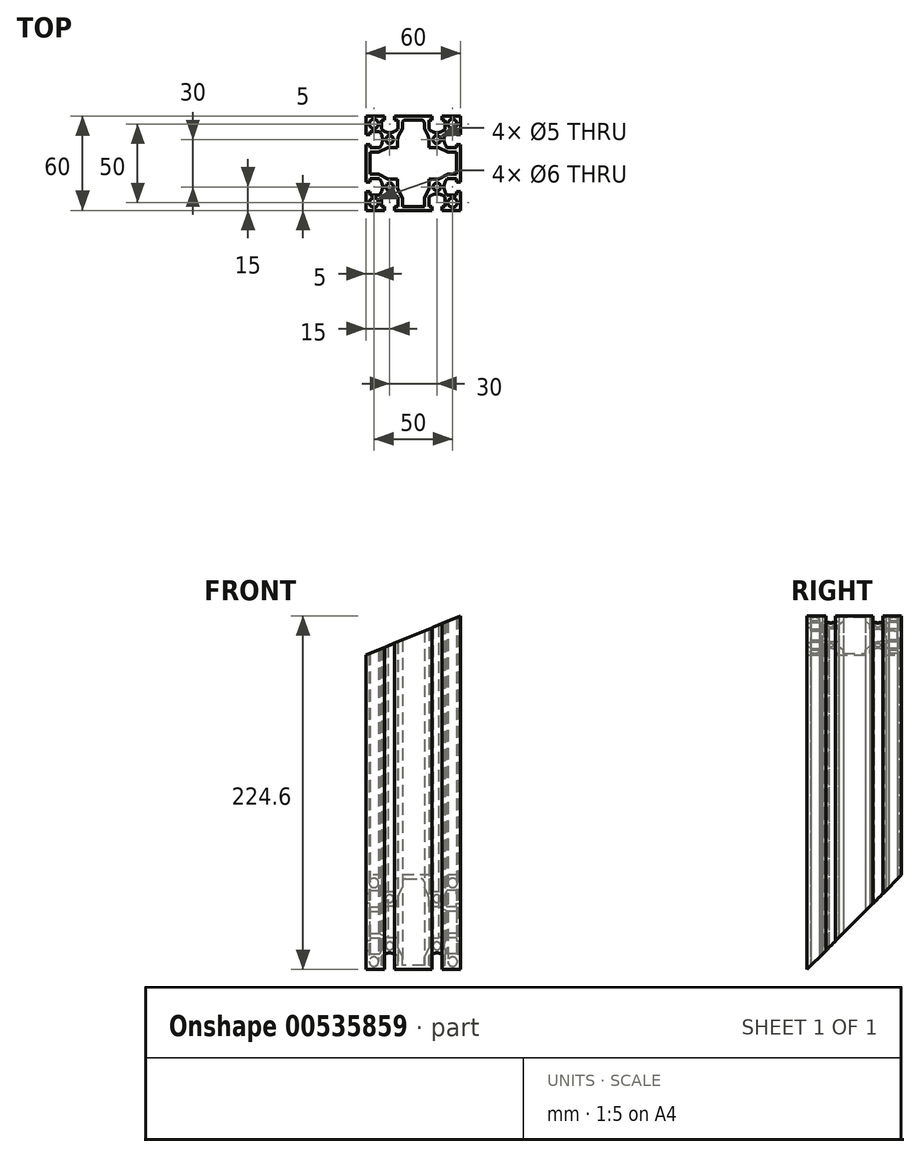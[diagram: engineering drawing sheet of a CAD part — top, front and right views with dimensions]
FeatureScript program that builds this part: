
annotation { "Feature Type Name" : "Feature", "Feature Type Description" : "" }
export const myFeature = defineFeature(function(context is Context, id is Id, definition is map)
    precondition{}
    {
        {
            var Q0;
            Q0=qCreatedBy(makeId("Top.planeOp"),FACE);
            var sketch = newSketch(context, id + "F0", { "sketchPlane" : qUnion([Q0])});
            skLineSegment(sketch, "E0.bottom", {"start": v(30, -30) * mm, "end": v(-30, -30) * mm});
            skLineSegment(sketch, "E0.top", {"start": v(30, 30) * mm, "end": v(-30, 30) * mm});
            skLineSegment(sketch, "E0.left", {"start": v(30, -30) * mm, "end": v(30, 30) * mm});
            skLineSegment(sketch, "E0.right", {"start": v(-30, -30) * mm, "end": v(-30, 30) * mm});
            skPoint(sketch, "E0.middle", {"position": v(0, 0) * mm});
            skLineSegment(sketch, "E1.top", {"start": v(-11.85, 30) * mm, "end": v(-18.15, 30) * mm});
            skLineSegment(sketch, "E1.left", {"start": v(-11.85, 27.5) * mm, "end": v(-11.85, 30) * mm});
            skLineSegment(sketch, "E1.right", {"start": v(-18.15, 27.5) * mm, "end": v(-18.15, 30) * mm});
            skPoint(sketch, "E1.middle", {"position": v(-15, 28.75) * mm});
            skLineSegment(sketch, "E2.bottom", {"start": v(-9.85, 27.5) * mm, "end": v(-11.85, 27.5) * mm});
            skLineSegment(sketch, "E2.left", {"start": v(-9.85, 27.5) * mm, "end": v(-9.85, 21.55) * mm});
            skLineSegment(sketch, "E2.right", {"start": v(-20.15, 27.5) * mm, "end": v(-20.15, 21.55) * mm});
            skPoint(sketch, "E2.middle", {"position": v(-15, 24.52) * mm});
            skArc(sketch, "E3", {"start": v(-20.15, 21.55) * mm, "mid": v(-15, 19.5) * mm, "end": v(-9.85, 21.55) * mm});
            skPoint(sketch, "E4.MirrorP", {"position": v(15, 24.52) * mm});
            skPoint(sketch, "E5.MirrorP", {"position": v(15, 28.75) * mm});
            skLineSegment(sketch, "E6.MirrorCS", {"start": v(11.85, 27.5) * mm, "end": v(11.85, 30) * mm});
            skLineSegment(sketch, "E7.MirrorCS", {"start": v(18.15, 27.5) * mm, "end": v(18.15, 30) * mm});
            skLineSegment(sketch, "E8.MirrorCS", {"start": v(9.85, 27.5) * mm, "end": v(11.85, 27.5) * mm});
            skLineSegment(sketch, "E9.MirrorCS", {"start": v(9.85, 27.5) * mm, "end": v(9.85, 21.55) * mm});
            skArc(sketch, "E10.MirrorCS", {"start": v(20.15, 21.55) * mm, "mid": v(15, 19.5) * mm, "end": v(9.85, 21.55) * mm});
            skLineSegment(sketch, "E11.MirrorCS", {"start": v(20.15, 27.5) * mm, "end": v(20.15, 21.55) * mm});
            skLineSegment(sketch, "E12.MirrorCS", {"start": v(11.85, 30) * mm, "end": v(18.15, 30) * mm});
            skLineSegment(sketch, "E13.1.0", {"start": v(27.5, 20.15) * mm, "end": v(21.55, 20.15) * mm});
            skLineSegment(sketch, "E13.1.1", {"start": v(27.5, 9.85) * mm, "end": v(21.55, 9.85) * mm});
            skArc(sketch, "E13.1.2", {"start": v(21.55, 20.15) * mm, "mid": v(19.5, 15) * mm, "end": v(21.55, 9.85) * mm});
            skLineSegment(sketch, "E13.1.3", {"start": v(27.5, -9.85) * mm, "end": v(21.55, -9.85) * mm});
            skLineSegment(sketch, "E13.1.4", {"start": v(27.5, -20.15) * mm, "end": v(21.55, -20.15) * mm});
            skPoint(sketch, "E13.1.5", {"position": v(28.75, 15) * mm});
            skPoint(sketch, "E13.1.6", {"position": v(28.75, -15) * mm});
            skArc(sketch, "E13.1.7", {"start": v(21.55, -20.15) * mm, "mid": v(19.5, -15) * mm, "end": v(21.55, -9.85) * mm});
            skPoint(sketch, "E13.1.8", {"position": v(24.52, -15) * mm});
            skPoint(sketch, "E13.1.9", {"position": v(24.52, 15) * mm});
            skLineSegment(sketch, "E13.1.10", {"start": v(27.5, 9.85) * mm, "end": v(27.5, 20.15) * mm});
            skLineSegment(sketch, "E13.1.11", {"start": v(27.5, -11.85) * mm, "end": v(27.5, -18.15) * mm});
            skLineSegment(sketch, "E13.1.12", {"start": v(30, 11.85) * mm, "end": v(30, 18.15) * mm});
            skLineSegment(sketch, "E13.1.13", {"start": v(30, -11.85) * mm, "end": v(30, -18.15) * mm});
            skLineSegment(sketch, "E13.1.14", {"start": v(27.5, 18.15) * mm, "end": v(30, 18.15) * mm});
            skLineSegment(sketch, "E13.1.15", {"start": v(27.5, 11.85) * mm, "end": v(30, 11.85) * mm});
            skLineSegment(sketch, "E13.1.16", {"start": v(27.5, 11.85) * mm, "end": v(27.5, 18.15) * mm});
            skLineSegment(sketch, "E13.1.17", {"start": v(27.5, -9.85) * mm, "end": v(27.5, -20.15) * mm});
            skLineSegment(sketch, "E13.1.18", {"start": v(27.5, -18.15) * mm, "end": v(30, -18.15) * mm});
            skLineSegment(sketch, "E13.1.19", {"start": v(27.5, -11.85) * mm, "end": v(30, -11.85) * mm});
            skLineSegment(sketch, "E13.2.0", {"start": v(20.15, -27.5) * mm, "end": v(20.15, -21.55) * mm});
            skLineSegment(sketch, "E13.2.1", {"start": v(9.85, -27.5) * mm, "end": v(9.85, -21.55) * mm});
            skArc(sketch, "E13.2.2", {"start": v(20.15, -21.55) * mm, "mid": v(15, -19.5) * mm, "end": v(9.85, -21.55) * mm});
            skLineSegment(sketch, "E13.2.3", {"start": v(-9.85, -27.5) * mm, "end": v(-9.85, -21.55) * mm});
            skLineSegment(sketch, "E13.2.4", {"start": v(-20.15, -27.5) * mm, "end": v(-20.15, -21.55) * mm});
            skPoint(sketch, "E13.2.5", {"position": v(15, -28.75) * mm});
            skPoint(sketch, "E13.2.6", {"position": v(-15, -28.75) * mm});
            skArc(sketch, "E13.2.7", {"start": v(-20.15, -21.55) * mm, "mid": v(-15, -19.5) * mm, "end": v(-9.85, -21.55) * mm});
            skPoint(sketch, "E13.2.8", {"position": v(-15, -24.52) * mm});
            skPoint(sketch, "E13.2.9", {"position": v(15, -24.52) * mm});
            skLineSegment(sketch, "E13.2.10", {"start": v(9.85, -27.5) * mm, "end": v(20.15, -27.5) * mm});
            skLineSegment(sketch, "E13.2.11", {"start": v(-11.85, -27.5) * mm, "end": v(-18.15, -27.5) * mm});
            skLineSegment(sketch, "E13.2.12", {"start": v(11.85, -30) * mm, "end": v(18.15, -30) * mm});
            skLineSegment(sketch, "E13.2.13", {"start": v(-11.85, -30) * mm, "end": v(-18.15, -30) * mm});
            skLineSegment(sketch, "E13.2.14", {"start": v(18.15, -27.5) * mm, "end": v(18.15, -30) * mm});
            skLineSegment(sketch, "E13.2.15", {"start": v(11.85, -27.5) * mm, "end": v(11.85, -30) * mm});
            skLineSegment(sketch, "E13.2.16", {"start": v(11.85, -27.5) * mm, "end": v(18.15, -27.5) * mm});
            skLineSegment(sketch, "E13.2.17", {"start": v(-9.85, -27.5) * mm, "end": v(-20.15, -27.5) * mm});
            skLineSegment(sketch, "E13.2.18", {"start": v(-18.15, -27.5) * mm, "end": v(-18.15, -30) * mm});
            skLineSegment(sketch, "E13.2.19", {"start": v(-11.85, -27.5) * mm, "end": v(-11.85, -30) * mm});
            skLineSegment(sketch, "E13.3.0", {"start": v(-27.5, -20.15) * mm, "end": v(-21.55, -20.15) * mm});
            skLineSegment(sketch, "E13.3.1", {"start": v(-27.5, -9.85) * mm, "end": v(-21.55, -9.85) * mm});
            skArc(sketch, "E13.3.2", {"start": v(-21.55, -20.15) * mm, "mid": v(-19.5, -15) * mm, "end": v(-21.55, -9.85) * mm});
            skLineSegment(sketch, "E13.3.3", {"start": v(-27.5, 9.85) * mm, "end": v(-21.55, 9.85) * mm});
            skLineSegment(sketch, "E13.3.4", {"start": v(-27.5, 20.15) * mm, "end": v(-21.55, 20.15) * mm});
            skPoint(sketch, "E13.3.5", {"position": v(-28.75, -15) * mm});
            skPoint(sketch, "E13.3.6", {"position": v(-28.75, 15) * mm});
            skArc(sketch, "E13.3.7", {"start": v(-21.55, 20.15) * mm, "mid": v(-19.5, 15) * mm, "end": v(-21.55, 9.85) * mm});
            skPoint(sketch, "E13.3.8", {"position": v(-24.52, 15) * mm});
            skPoint(sketch, "E13.3.9", {"position": v(-24.52, -15) * mm});
            skLineSegment(sketch, "E13.3.10", {"start": v(-27.5, -9.85) * mm, "end": v(-27.5, -20.15) * mm});
            skLineSegment(sketch, "E13.3.11", {"start": v(-27.5, 11.85) * mm, "end": v(-27.5, 18.15) * mm});
            skLineSegment(sketch, "E13.3.12", {"start": v(-30, -11.85) * mm, "end": v(-30, -18.15) * mm});
            skLineSegment(sketch, "E13.3.13", {"start": v(-30, 11.85) * mm, "end": v(-30, 18.15) * mm});
            skLineSegment(sketch, "E13.3.14", {"start": v(-27.5, -18.15) * mm, "end": v(-30, -18.15) * mm});
            skLineSegment(sketch, "E13.3.15", {"start": v(-27.5, -11.85) * mm, "end": v(-30, -11.85) * mm});
            skLineSegment(sketch, "E13.3.16", {"start": v(-27.5, -11.85) * mm, "end": v(-27.5, -18.15) * mm});
            skLineSegment(sketch, "E13.3.17", {"start": v(-27.5, 9.85) * mm, "end": v(-27.5, 20.15) * mm});
            skLineSegment(sketch, "E13.3.18", {"start": v(-27.5, 18.15) * mm, "end": v(-30, 18.15) * mm});
            skLineSegment(sketch, "E13.3.19", {"start": v(-27.5, 11.85) * mm, "end": v(-30, 11.85) * mm});
            skLineSegment(sketch, "E13.anchor1", {"start": v(0, 0) * mm, "end": v(-20.15, 21.55) * mm, "construction": true});
            skLineSegment(sketch, "E13.anchor2", {"start": v(0, 0) * mm, "end": v(-21.55, -20.15) * mm, "construction": true});
            skLineSegment(sketch, "E14.trimOffspring", {"start": v(-18.15, 27.5) * mm, "end": v(-20.15, 27.5) * mm});
            skLineSegment(sketch, "E15.trimOffspring", {"start": v(18.15, 27.5) * mm, "end": v(20.15, 27.5) * mm});
            skCircle(sketch, "E16", {"center": v(-15, 15) * mm, "radius": 2.5 * mm});
            skCircle(sketch, "E17", {"center": v(-25, 25) * mm, "radius": 3 * mm});
            skCircle(sketch, "E18.MirrorC", {"center": v(25, 25) * mm, "radius": 3 * mm});
            skCircle(sketch, "E19.MirrorC", {"center": v(25, -25) * mm, "radius": 3 * mm});
            skCircle(sketch, "E20.MirrorC", {"center": v(-25, -25) * mm, "radius": 3 * mm});
            skCircle(sketch, "E21.MirrorC", {"center": v(15, 15) * mm, "radius": 2.5 * mm});
            skCircle(sketch, "E22.MirrorC", {"center": v(15, -15) * mm, "radius": 2.5 * mm});
            skCircle(sketch, "E23.MirrorC", {"center": v(-15, -15) * mm, "radius": 2.5 * mm});
            skLineSegment(sketch, "E24", {"start": v(-7, 27.5) * mm, "end": v(0, 27.5) * mm});
            skLineSegment(sketch, "E25", {"start": v(-7, 27.5) * mm, "end": v(-7, 22) * mm});
            skLineSegment(sketch, "E26", {"start": v(-10, 10) * mm, "end": v(-10, 16) * mm});
            skLineSegment(sketch, "E27", {"start": v(-10, 16) * mm, "end": v(-7, 22) * mm});
            skLineSegment(sketch, "E28.MirrorCS", {"start": v(10, 10) * mm, "end": v(10, 16) * mm});
            skLineSegment(sketch, "E29.MirrorCS", {"start": v(10, 16) * mm, "end": v(7, 22) * mm});
            skLineSegment(sketch, "E30.MirrorCS", {"start": v(7, 27.5) * mm, "end": v(0, 27.5) * mm});
            skLineSegment(sketch, "E31.MirrorCS", {"start": v(7, 27.5) * mm, "end": v(7, 22) * mm});
            skLineSegment(sketch, "E32.1.0", {"start": v(-10, -10) * mm, "end": v(-16, -10) * mm});
            skLineSegment(sketch, "E32.1.1", {"start": v(-16, -10) * mm, "end": v(-22, -7) * mm});
            skLineSegment(sketch, "E32.1.2", {"start": v(-27.5, -7) * mm, "end": v(-22, -7) * mm});
            skLineSegment(sketch, "E32.1.3", {"start": v(-27.5, -7) * mm, "end": v(-27.5, 0) * mm});
            skLineSegment(sketch, "E32.1.4", {"start": v(-27.5, 7) * mm, "end": v(-27.5, 0) * mm});
            skLineSegment(sketch, "E32.1.5", {"start": v(-27.5, 7) * mm, "end": v(-22, 7) * mm});
            skLineSegment(sketch, "E32.1.6", {"start": v(-16, 10) * mm, "end": v(-22, 7) * mm});
            skLineSegment(sketch, "E32.1.7", {"start": v(-10, 10) * mm, "end": v(-16, 10) * mm});
            skLineSegment(sketch, "E32.2.0", {"start": v(10, -10) * mm, "end": v(10, -16) * mm});
            skLineSegment(sketch, "E32.2.1", {"start": v(10, -16) * mm, "end": v(7, -22) * mm});
            skLineSegment(sketch, "E32.2.2", {"start": v(7, -27.5) * mm, "end": v(7, -22) * mm});
            skLineSegment(sketch, "E32.2.3", {"start": v(7, -27.5) * mm, "end": v(0, -27.5) * mm});
            skLineSegment(sketch, "E32.2.4", {"start": v(-7, -27.5) * mm, "end": v(0, -27.5) * mm});
            skLineSegment(sketch, "E32.2.5", {"start": v(-7, -27.5) * mm, "end": v(-7, -22) * mm});
            skLineSegment(sketch, "E32.2.6", {"start": v(-10, -16) * mm, "end": v(-7, -22) * mm});
            skLineSegment(sketch, "E32.2.7", {"start": v(-10, -10) * mm, "end": v(-10, -16) * mm});
            skLineSegment(sketch, "E32.3.0", {"start": v(10, 10) * mm, "end": v(16, 10) * mm});
            skLineSegment(sketch, "E32.3.1", {"start": v(16, 10) * mm, "end": v(22, 7) * mm});
            skLineSegment(sketch, "E32.3.2", {"start": v(27.5, 7) * mm, "end": v(22, 7) * mm});
            skLineSegment(sketch, "E32.3.3", {"start": v(27.5, 7) * mm, "end": v(27.5, 0) * mm});
            skLineSegment(sketch, "E32.3.4", {"start": v(27.5, -7) * mm, "end": v(27.5, 0) * mm});
            skLineSegment(sketch, "E32.3.5", {"start": v(27.5, -7) * mm, "end": v(22, -7) * mm});
            skLineSegment(sketch, "E32.3.6", {"start": v(16, -10) * mm, "end": v(22, -7) * mm});
            skLineSegment(sketch, "E32.3.7", {"start": v(10, -10) * mm, "end": v(16, -10) * mm});
            skSolve(sketch);
        }
        {
            var Q0;
            {var subQ30=sQuery(id+"F0.wireOp",EDGE,"E1.left");Q0=makeQuery(id+"F0.imprint","IMPRINT",FACE,{"disambiguationData":[TD([[makeQuery(id+"F0.imprint","IMPRINT",EDGE,{"derivedFrom":subQ30}),-1.0]])]});}
            extrude(context, id + "F1", {"entities" : qUnion([Q0]), "depth" : 224.6 * mm, "offsetDistance" : 25 * mm});
        }
        {
            var Q0;
            Q0=makeQuery(id+"F1.opExtrude","SWEPT_EDGE",EDGE,{"disambiguationData":[OSD([sQuery(id+"F0.wireOp",EDGE,"E24"),sQuery(id+"F0.wireOp",EDGE,"E25")])]});
            var Q1;
            Q1=makeQuery(id+"F1.opExtrude","SWEPT_EDGE",EDGE,{"disambiguationData":[OSD([sQuery(id+"F0.wireOp",EDGE,"E30.MirrorCS"),sQuery(id+"F0.wireOp",EDGE,"E31.MirrorCS")])]});
            var Q2;
            Q2=makeQuery(id+"F1.opExtrude","SWEPT_EDGE",EDGE,{"disambiguationData":[OSD([sQuery(id+"F0.wireOp",EDGE,"840db5bc-c403-45cd-90c7-254e62d9e8c5.3.2"),sQuery(id+"F0.wireOp",EDGE,"840db5bc-c403-45cd-90c7-254e62d9e8c5.3.3")])]});
            var Q3;
            Q3=makeQuery(id+"F1.opExtrude","SWEPT_EDGE",EDGE,{"disambiguationData":[OSD([sQuery(id+"F0.wireOp",EDGE,"840db5bc-c403-45cd-90c7-254e62d9e8c5.3.4"),sQuery(id+"F0.wireOp",EDGE,"840db5bc-c403-45cd-90c7-254e62d9e8c5.3.5")])]});
            var Q4;
            Q4=makeQuery(id+"F1.opExtrude","SWEPT_EDGE",EDGE,{"disambiguationData":[OSD([sQuery(id+"F0.wireOp",EDGE,"840db5bc-c403-45cd-90c7-254e62d9e8c5.1.4"),sQuery(id+"F0.wireOp",EDGE,"840db5bc-c403-45cd-90c7-254e62d9e8c5.1.5")])]});
            var Q5;
            Q5=makeQuery(id+"F1.opExtrude","SWEPT_EDGE",EDGE,{"disambiguationData":[OSD([sQuery(id+"F0.wireOp",EDGE,"840db5bc-c403-45cd-90c7-254e62d9e8c5.1.2"),sQuery(id+"F0.wireOp",EDGE,"840db5bc-c403-45cd-90c7-254e62d9e8c5.1.3")])]});
            var Q6;
            Q6=makeQuery(id+"F1.opExtrude","SWEPT_EDGE",EDGE,{"disambiguationData":[OSD([sQuery(id+"F0.wireOp",EDGE,"840db5bc-c403-45cd-90c7-254e62d9e8c5.2.2"),sQuery(id+"F0.wireOp",EDGE,"840db5bc-c403-45cd-90c7-254e62d9e8c5.2.3")])]});
            var Q7;
            Q7=makeQuery(id+"F1.opExtrude","SWEPT_EDGE",EDGE,{"disambiguationData":[OSD([sQuery(id+"F0.wireOp",EDGE,"840db5bc-c403-45cd-90c7-254e62d9e8c5.2.4"),sQuery(id+"F0.wireOp",EDGE,"840db5bc-c403-45cd-90c7-254e62d9e8c5.2.5")])]});
            fillet(context, id + "F2", {"entities" : qUnion([Q0, Q1, Q2, Q3, Q4, Q5, Q6, Q7]), "radius" : 2 * mm, "tangentPropagation" : true, "allowEdgeOverflow" : false});
        }
        {
            var Q0;
            Q0=makeQuery(id+"F1.opExtrude","SWEPT_EDGE",EDGE,{"disambiguationData":[OSD([sQuery(id+"F0.wireOp",EDGE,"E26"),sQuery(id+"F0.wireOp",EDGE,"E27")])]});
            var Q1;
            Q1=makeQuery(id+"F1.opExtrude","SWEPT_EDGE",EDGE,{"disambiguationData":[OSD([sQuery(id+"F0.wireOp",EDGE,"E28.MirrorCS"),sQuery(id+"F0.wireOp",EDGE,"E29.MirrorCS")])]});
            var Q2;
            Q2=makeQuery(id+"F1.opExtrude","SWEPT_EDGE",EDGE,{"disambiguationData":[OSD([sQuery(id+"F0.wireOp",EDGE,"840db5bc-c403-45cd-90c7-254e62d9e8c5.3.0"),sQuery(id+"F0.wireOp",EDGE,"840db5bc-c403-45cd-90c7-254e62d9e8c5.3.1")])]});
            var Q3;
            Q3=makeQuery(id+"F1.opExtrude","SWEPT_EDGE",EDGE,{"disambiguationData":[OSD([sQuery(id+"F0.wireOp",EDGE,"840db5bc-c403-45cd-90c7-254e62d9e8c5.1.6"),sQuery(id+"F0.wireOp",EDGE,"840db5bc-c403-45cd-90c7-254e62d9e8c5.1.7")])]});
            var Q4;
            Q4=makeQuery(id+"F1.opExtrude","SWEPT_EDGE",EDGE,{"disambiguationData":[OSD([sQuery(id+"F0.wireOp",EDGE,"840db5bc-c403-45cd-90c7-254e62d9e8c5.1.0"),sQuery(id+"F0.wireOp",EDGE,"840db5bc-c403-45cd-90c7-254e62d9e8c5.1.1")])]});
            var Q5;
            Q5=makeQuery(id+"F1.opExtrude","SWEPT_EDGE",EDGE,{"disambiguationData":[OSD([sQuery(id+"F0.wireOp",EDGE,"840db5bc-c403-45cd-90c7-254e62d9e8c5.3.6"),sQuery(id+"F0.wireOp",EDGE,"840db5bc-c403-45cd-90c7-254e62d9e8c5.3.7")])]});
            var Q6;
            Q6=makeQuery(id+"F1.opExtrude","SWEPT_EDGE",EDGE,{"disambiguationData":[OSD([sQuery(id+"F0.wireOp",EDGE,"840db5bc-c403-45cd-90c7-254e62d9e8c5.2.0"),sQuery(id+"F0.wireOp",EDGE,"840db5bc-c403-45cd-90c7-254e62d9e8c5.2.1")])]});
            var Q7;
            Q7=makeQuery(id+"F1.opExtrude","SWEPT_EDGE",EDGE,{"disambiguationData":[OSD([sQuery(id+"F0.wireOp",EDGE,"840db5bc-c403-45cd-90c7-254e62d9e8c5.2.6"),sQuery(id+"F0.wireOp",EDGE,"840db5bc-c403-45cd-90c7-254e62d9e8c5.2.7")])]});
            fillet(context, id + "F3", {"entities" : qUnion([Q0, Q1, Q2, Q3, Q4, Q5, Q6, Q7]), "radius" : 7 * mm, "tangentPropagation" : true, "allowEdgeOverflow" : false});
        }
        {
            var Q0;
            {var subQ0=sQuery(id+"F0.wireOp",EDGE,"E0.bottom");Q0=makeQuery(id+"F1.opExtrude","SWEPT_FACE",FACE,{"disambiguationData":[OSD([subQ0]),TDD([makeQuery(id+"F0.imprint","IMPRINT",EDGE,{"disambiguationData":[TD([[makeQuery(id+"F0.imprint","INTERSECT",VERTEX,{"derivedFrom":[subQ0,sQuery(id+"F0.wireOp",EDGE,"E13.2.12"),sQuery(id+"F0.wireOp",EDGE,"E13.2.15")]}),-1.0]])],"derivedFrom":subQ0})])]});}
            var sketch = newSketch(context, id + "F4", { "sketchPlane" : qUnion([Q0])});
            skLineSegment(sketch, "E33.0", {"start": v(-18.15, 224.6) * mm, "end": v(-30, 224.6) * mm});
            skLineSegment(sketch, "E33.1", {"start": v(30, 224.6) * mm, "end": v(30, 0) * mm});
            skLineSegment(sketch, "E34", {"start": v(-30, 224.6) * mm, "end": v(30, 224.6) * mm});
            skLineSegment(sketch, "E35", {"start": v(30, 164.6) * mm, "end": v(-30, 224.6) * mm});
            skLineSegment(sketch, "E36.0", {"start": v(-18.15, 0) * mm, "end": v(-30, 0) * mm});
            skLineSegment(sketch, "E37", {"start": v(-30, 0) * mm, "end": v(30, 0) * mm});
            skLineSegment(sketch, "E38", {"start": v(30, 60) * mm, "end": v(-30, 0) * mm});
            skSolve(sketch);
        }
        {
            var Q0;
            Q0=qCreatedBy(makeId("Right.planeOp"),FACE);
            var sketch = newSketch(context, id + "F5", { "sketchPlane" : qUnion([Q0])});
            skLineSegment(sketch, "E39.bottom", {"start": v(211.64, 40.85) * mm, "end": v(111.25, 141.25) * mm});
            skLineSegment(sketch, "E39.top", {"start": v(70.4, -100.4) * mm, "end": v(-30, 0) * mm});
            skLineSegment(sketch, "E39.left", {"start": v(211.64, 40.85) * mm, "end": v(70.4, -100.4) * mm});
            skLineSegment(sketch, "E39.right", {"start": v(111.25, 141.25) * mm, "end": v(-30, 0) * mm});
            skSolve(sketch);
        }
        {
            var Q0;
            Q0=qSketchRegion(id+"F5",true);
            extrude(context, id + "F6", {"entities" : qUnion([Q0]), "operationType" : NewBodyOperationType.REMOVE, "oppositeDirection" : true, "depth" : 30 * mm, "offsetDistance" : 25 * mm, "hasSecondDirection" : true, "secondDirectionOppositeDirection" : false, "secondDirectionDepth" : 30 * mm});
        }
        {
            var Q0;
            Q0=qCreatedBy(makeId("Front.planeOp"),FACE);
            var sketch = newSketch(context, id + "F7", { "sketchPlane" : qUnion([Q0])});
            skLineSegment(sketch, "E40.bottom", {"start": v(-136.09, 331.44) * mm, "end": v(-32.1, 374.51) * mm});
            skLineSegment(sketch, "E40.top", {"start": v(-74, 181.53) * mm, "end": v(30, 224.6) * mm});
            skLineSegment(sketch, "E40.left", {"start": v(-136.09, 331.44) * mm, "end": v(-74, 181.53) * mm});
            skLineSegment(sketch, "E40.right", {"start": v(-32.1, 374.51) * mm, "end": v(30, 224.6) * mm});
            skSolve(sketch);
        }
        {
            var Q0;
            Q0=qSketchRegion(id+"F7",true);
            extrude(context, id + "F8", {"entities" : qUnion([Q0]), "operationType" : NewBodyOperationType.REMOVE, "depth" : 30 * mm, "offsetDistance" : 25 * mm, "hasSecondDirection" : true, "secondDirectionOppositeDirection" : true, "secondDirectionDepth" : 30 * mm});
        }
    });
